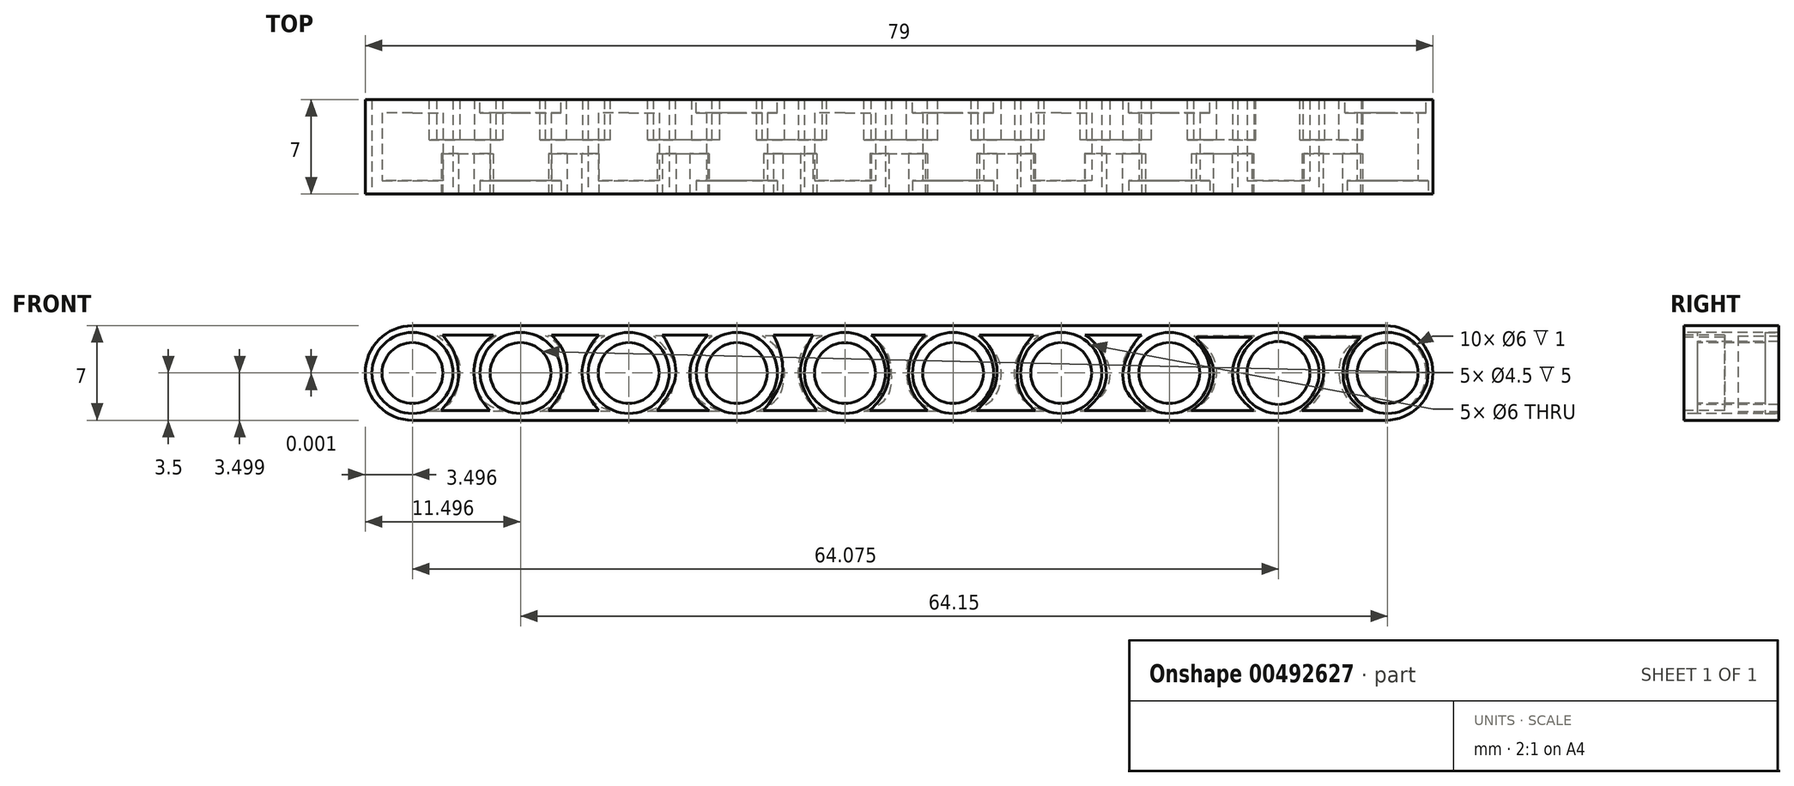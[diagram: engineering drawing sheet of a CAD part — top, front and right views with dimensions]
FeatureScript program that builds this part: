
annotation { "Feature Type Name" : "Feature", "Feature Type Description" : "" }
export const myFeature = defineFeature(function(context is Context, id is Id, definition is map)
    precondition{}
    {
        {
            var Q0;
            Q0=qCreatedBy(makeId("Front.planeOp"),FACE);
            var sketch = newSketch(context, id + "F0", { "sketchPlane" : qUnion([Q0])});
            skLineSegment(sketch, "E0", {"start": v(-57.43, 7) * mm, "end": v(21.57, 7) * mm});
            skLineSegment(sketch, "E1", {"start": v(21.57, 7) * mm, "end": v(21.57, 0) * mm});
            skLineSegment(sketch, "E2", {"start": v(21.57, 0) * mm, "end": v(-57.43, 0) * mm});
            skLineSegment(sketch, "E3", {"start": v(-57.43, 0) * mm, "end": v(-57.43, 7) * mm});
            skLineSegment(sketch, "E4", {"start": v(-62.57, 3.5) * mm, "end": v(30.14, 3.5) * mm, "construction": true});
            skPoint(sketch, "E4.startSnap0", {"position": v(-57.43, 3.5) * mm});
            skPoint(sketch, "E4.endSnap0", {"position": v(21.57, 3.5) * mm});
            skSolve(sketch);
        }
        {
            var Q0;
            Q0 = qSketchRegion(id + "F0", true);
            extrude(context, id + "F1", {"entities" : qUnion([Q0]), "depth" : 7 * mm});
        }
        {
            var Q0;
            Q0=makeQuery(id+"F1.opExtrude","CAP_FACE",FACE,{"disambiguationData":[OSD([sQuery(id+"F0.wireOp",EDGE,"E0"),sQuery(id+"F0.wireOp",EDGE,"E1"),sQuery(id+"F0.wireOp",EDGE,"E2"),sQuery(id+"F0.wireOp",EDGE,"E3")])],"isStart":false});
            var sketch = newSketch(context, id + "F2", { "sketchPlane" : qUnion([Q0])});
            skPoint(sketch, "E5.startSnap0", {"position": v(-57.43, 3.5) * mm});
            skPoint(sketch, "E5.endSnap0", {"position": v(21.57, 3.5) * mm});
            skCircle(sketch, "E6", {"center": v(18.22, 3.5) * mm, "radius": 2.25 * mm});
            skCircle(sketch, "E7.MirrorC", {"center": v(10.14, 3.5) * mm, "radius": 2.32 * mm});
            skCircle(sketch, "E8.MirrorC", {"center": v(2.07, 3.5) * mm, "radius": 2.25 * mm});
            skCircle(sketch, "E9.MirrorC", {"center": v(-5.93, 3.5) * mm, "radius": 2.25 * mm});
            skCircle(sketch, "E10.MirrorC", {"center": v(-13.93, 3.5) * mm, "radius": 2.25 * mm});
            skCircle(sketch, "E11.MirrorC", {"center": v(-21.93, 3.5) * mm, "radius": 2.25 * mm});
            skCircle(sketch, "E12.MirrorC", {"center": v(-29.93, 3.5) * mm, "radius": 2.25 * mm});
            skCircle(sketch, "E13.MirrorC", {"center": v(-37.93, 3.5) * mm, "radius": 2.25 * mm});
            skCircle(sketch, "E14.MirrorC", {"center": v(-45.93, 3.5) * mm, "radius": 2.25 * mm});
            skCircle(sketch, "E15.MirrorC", {"center": v(-53.93, 3.5) * mm, "radius": 2.25 * mm});
            skCircle(sketch, "E16", {"center": v(18.22, 3.5) * mm, "radius": 3 * mm});
            skCircle(sketch, "E17", {"center": v(10.14, 3.5) * mm, "radius": 3 * mm});
            skCircle(sketch, "E18", {"center": v(2.07, 3.5) * mm, "radius": 3 * mm});
            skCircle(sketch, "E19", {"center": v(-5.93, 3.5) * mm, "radius": 3 * mm});
            skCircle(sketch, "E20", {"center": v(-13.93, 3.5) * mm, "radius": 3 * mm});
            skCircle(sketch, "E21", {"center": v(-21.93, 3.5) * mm, "radius": 3 * mm});
            skCircle(sketch, "E22", {"center": v(-29.93, 3.5) * mm, "radius": 3 * mm});
            skCircle(sketch, "E23", {"center": v(-37.93, 3.5) * mm, "radius": 3 * mm});
            skCircle(sketch, "E24", {"center": v(-45.93, 3.5) * mm, "radius": 3 * mm});
            skCircle(sketch, "E25", {"center": v(-53.93, 3.5) * mm, "radius": 3 * mm});
            skSolve(sketch);
        }
        {
            var Q0;
            Q0=makeQuery(id+"F2.imprint","IMPRINT",FACE,{"disambiguationData":[TD([[makeQuery(id+"F2.imprint","IMPRINT",EDGE,{"derivedFrom":sQuery(id+"F2.wireOp",EDGE,"E6")}),-1.0]])]});
            var sketch = newSketch(context, id + "F3", { "sketchPlane" : qUnion([Q0])});
            skSolve(sketch);
        }
        {
            var Q0;
            Q0=makeQuery(id+"F2.imprint","IMPRINT",FACE,{"disambiguationData":[TD([[makeQuery(id+"F2.imprint","IMPRINT",EDGE,{"derivedFrom":sQuery(id+"F2.wireOp",EDGE,"E6")}),-1.0]])]});
            var Q1;
            Q1=makeQuery(id+"F2.imprint","IMPRINT",FACE,{"disambiguationData":[TD([[makeQuery(id+"F2.imprint","IMPRINT",EDGE,{"derivedFrom":sQuery(id+"F2.wireOp",EDGE,"E7.MirrorC")}),1.0]])]});
            var Q2;
            Q2=makeQuery(id+"F2.imprint","IMPRINT",FACE,{"disambiguationData":[TD([[makeQuery(id+"F2.imprint","IMPRINT",EDGE,{"derivedFrom":sQuery(id+"F2.wireOp",EDGE,"E8.MirrorC")}),-1.0]])]});
            var Q3;
            Q3=makeQuery(id+"F2.imprint","IMPRINT",FACE,{"disambiguationData":[TD([[makeQuery(id+"F2.imprint","IMPRINT",EDGE,{"derivedFrom":sQuery(id+"F2.wireOp",EDGE,"E9.MirrorC")}),1.0]])]});
            var Q4;
            Q4=makeQuery(id+"F2.imprint","IMPRINT",FACE,{"disambiguationData":[TD([[makeQuery(id+"F2.imprint","IMPRINT",EDGE,{"derivedFrom":sQuery(id+"F2.wireOp",EDGE,"E10.MirrorC")}),-1.0]])]});
            var Q5;
            Q5=makeQuery(id+"F2.imprint","IMPRINT",FACE,{"disambiguationData":[TD([[makeQuery(id+"F2.imprint","IMPRINT",EDGE,{"derivedFrom":sQuery(id+"F2.wireOp",EDGE,"E11.MirrorC")}),1.0]])]});
            var Q6;
            Q6=makeQuery(id+"F2.imprint","IMPRINT",FACE,{"disambiguationData":[TD([[makeQuery(id+"F2.imprint","IMPRINT",EDGE,{"derivedFrom":sQuery(id+"F2.wireOp",EDGE,"E12.MirrorC")}),-1.0]])]});
            var Q7;
            Q7=makeQuery(id+"F2.imprint","IMPRINT",FACE,{"disambiguationData":[TD([[makeQuery(id+"F2.imprint","IMPRINT",EDGE,{"derivedFrom":sQuery(id+"F2.wireOp",EDGE,"E13.MirrorC")}),1.0]])]});
            var Q8;
            Q8=makeQuery(id+"F2.imprint","IMPRINT",FACE,{"disambiguationData":[TD([[makeQuery(id+"F2.imprint","IMPRINT",EDGE,{"derivedFrom":sQuery(id+"F2.wireOp",EDGE,"E14.MirrorC")}),-1.0]])]});
            var Q9;
            Q9=makeQuery(id+"F2.imprint","IMPRINT",FACE,{"disambiguationData":[TD([[makeQuery(id+"F2.imprint","IMPRINT",EDGE,{"derivedFrom":sQuery(id+"F2.wireOp",EDGE,"E15.MirrorC")}),1.0]])]});
            extrude(context, id + "F4", {"entities" : qUnion([Q0, Q1, Q2, Q3, Q4, Q5, Q6, Q7, Q8, Q9]), "operationType" : NewBodyOperationType.REMOVE, "oppositeDirection" : true, "depth" : 1 * mm});
        }
        {
            var Q0;
            Q0=makeQuery(id+"F2.imprint","IMPRINT",FACE,{"disambiguationData":[TD([[makeQuery(id+"F2.imprint","IMPRINT",EDGE,{"derivedFrom":sQuery(id+"F2.wireOp",EDGE,"E15.MirrorC")}),-1.0]])]});
            var Q1;
            Q1=makeQuery(id+"F2.imprint","IMPRINT",FACE,{"disambiguationData":[TD([[makeQuery(id+"F2.imprint","IMPRINT",EDGE,{"derivedFrom":sQuery(id+"F2.wireOp",EDGE,"E14.MirrorC")}),1.0]])]});
            var Q2;
            Q2=makeQuery(id+"F2.imprint","IMPRINT",FACE,{"disambiguationData":[TD([[makeQuery(id+"F2.imprint","IMPRINT",EDGE,{"derivedFrom":sQuery(id+"F2.wireOp",EDGE,"E13.MirrorC")}),-1.0]])]});
            var Q3;
            Q3=makeQuery(id+"F2.imprint","IMPRINT",FACE,{"disambiguationData":[TD([[makeQuery(id+"F2.imprint","IMPRINT",EDGE,{"derivedFrom":sQuery(id+"F2.wireOp",EDGE,"E12.MirrorC")}),1.0]])]});
            var Q4;
            Q4=makeQuery(id+"F2.imprint","IMPRINT",FACE,{"disambiguationData":[TD([[makeQuery(id+"F2.imprint","IMPRINT",EDGE,{"derivedFrom":sQuery(id+"F2.wireOp",EDGE,"E11.MirrorC")}),-1.0]])]});
            var Q5;
            Q5=makeQuery(id+"F2.imprint","IMPRINT",FACE,{"disambiguationData":[TD([[makeQuery(id+"F2.imprint","IMPRINT",EDGE,{"derivedFrom":sQuery(id+"F2.wireOp",EDGE,"E10.MirrorC")}),1.0]])]});
            var Q6;
            Q6=makeQuery(id+"F2.imprint","IMPRINT",FACE,{"disambiguationData":[TD([[makeQuery(id+"F2.imprint","IMPRINT",EDGE,{"derivedFrom":sQuery(id+"F2.wireOp",EDGE,"E9.MirrorC")}),-1.0]])]});
            var Q7;
            Q7=makeQuery(id+"F2.imprint","IMPRINT",FACE,{"disambiguationData":[TD([[makeQuery(id+"F2.imprint","IMPRINT",EDGE,{"derivedFrom":sQuery(id+"F2.wireOp",EDGE,"E8.MirrorC")}),1.0]])]});
            var Q8;
            Q8=makeQuery(id+"F2.imprint","IMPRINT",FACE,{"disambiguationData":[TD([[makeQuery(id+"F2.imprint","IMPRINT",EDGE,{"derivedFrom":sQuery(id+"F2.wireOp",EDGE,"E7.MirrorC")}),-1.0]])]});
            var Q9;
            Q9=makeQuery(id+"F2.imprint","IMPRINT",FACE,{"disambiguationData":[TD([[makeQuery(id+"F2.imprint","IMPRINT",EDGE,{"derivedFrom":sQuery(id+"F2.wireOp",EDGE,"E6")}),1.0]])]});
            extrude(context, id + "F5", {"entities" : qUnion([Q0, Q1, Q2, Q3, Q4, Q5, Q6, Q7, Q8, Q9]), "operationType" : NewBodyOperationType.REMOVE, "oppositeDirection" : true, "depth" : 8 * mm});
        }
        {
            var Q0;
            Q0=makeQuery(id+"F1.opExtrude","SWEPT_EDGE",EDGE,{"disambiguationData":[OSD([sQuery(id+"F0.wireOp",EDGE,"E0"),sQuery(id+"F0.wireOp",EDGE,"E1")])]});
            var Q1;
            Q1=makeQuery(id+"F1.opExtrude","SWEPT_EDGE",EDGE,{"disambiguationData":[OSD([sQuery(id+"F0.wireOp",EDGE,"E0"),sQuery(id+"F0.wireOp",EDGE,"E3")])]});
            var Q2;
            Q2=makeQuery(id+"F1.opExtrude","SWEPT_EDGE",EDGE,{"disambiguationData":[OSD([sQuery(id+"F0.wireOp",EDGE,"E1"),sQuery(id+"F0.wireOp",EDGE,"E2")])]});
            var Q3;
            Q3=makeQuery(id+"F1.opExtrude","SWEPT_EDGE",EDGE,{"disambiguationData":[OSD([sQuery(id+"F0.wireOp",EDGE,"E2"),sQuery(id+"F0.wireOp",EDGE,"E3")])]});
            fillet(context, id + "F6", {"entities" : qUnion([Q0, Q1, Q2, Q3]), "radius" : 3.5 * mm, "tangentPropagation" : true, "allowEdgeOverflow" : false});
        }
        {
            var Q0;
            Q0=makeQuery(id+"F1.opExtrude","CAP_FACE",FACE,{"disambiguationData":[OSD([sQuery(id+"F0.wireOp",EDGE,"E0"),sQuery(id+"F0.wireOp",EDGE,"E1"),sQuery(id+"F0.wireOp",EDGE,"E2"),sQuery(id+"F0.wireOp",EDGE,"E3")])],"isStart":true});
            var sketch = newSketch(context, id + "F7", { "sketchPlane" : qUnion([Q0])});
            skPoint(sketch, "E26", {"position": v(-10.14, 3.5) * mm});
            skPoint(sketch, "E27", {"position": v(-2.07, 3.5) * mm});
            skPoint(sketch, "E28", {"position": v(5.93, 3.5) * mm});
            skPoint(sketch, "E29", {"position": v(13.93, 3.5) * mm});
            skPoint(sketch, "E30", {"position": v(21.93, 3.5) * mm});
            skPoint(sketch, "E31", {"position": v(29.93, 3.5) * mm});
            skPoint(sketch, "E32", {"position": v(37.93, 3.5) * mm});
            skPoint(sketch, "E33", {"position": v(45.93, 3.5) * mm});
            skPoint(sketch, "E34", {"position": v(53.93, 3.5) * mm});
            skPoint(sketch, "E35", {"position": v(-18.07, 3.5) * mm});
            skCircle(sketch, "E36", {"center": v(-18.07, 3.5) * mm, "radius": 3 * mm});
            skCircle(sketch, "E37", {"center": v(-10.14, 3.5) * mm, "radius": 3 * mm});
            skCircle(sketch, "E38", {"center": v(-2.07, 3.5) * mm, "radius": 3 * mm});
            skCircle(sketch, "E39", {"center": v(5.93, 3.5) * mm, "radius": 3 * mm});
            skCircle(sketch, "E40", {"center": v(13.93, 3.5) * mm, "radius": 3 * mm});
            skCircle(sketch, "E41", {"center": v(21.93, 3.5) * mm, "radius": 3 * mm});
            skCircle(sketch, "E42", {"center": v(29.93, 3.5) * mm, "radius": 3 * mm});
            skCircle(sketch, "E43", {"center": v(37.93, 3.5) * mm, "radius": 3 * mm});
            skCircle(sketch, "E44", {"center": v(45.93, 3.5) * mm, "radius": 3 * mm});
            skCircle(sketch, "E45", {"center": v(53.93, 3.5) * mm, "radius": 3 * mm});
            skSolve(sketch);
        }
        {
            var Q0;
            Q0=makeQuery(id+"F7.imprint","IMPRINT",FACE,{"disambiguationData":[TD([[makeQuery(id+"F7.imprint","IMPRINT",EDGE,{"derivedFrom":sQuery(id+"F7.wireOp",EDGE,"E36")}),1.0]])]});
            var Q1;
            Q1=makeQuery(id+"F7.imprint","IMPRINT",FACE,{"disambiguationData":[TD([[makeQuery(id+"F7.imprint","IMPRINT",EDGE,{"derivedFrom":sQuery(id+"F7.wireOp",EDGE,"E37")}),1.0]])]});
            var Q2;
            Q2=makeQuery(id+"F7.imprint","IMPRINT",FACE,{"disambiguationData":[TD([[makeQuery(id+"F7.imprint","IMPRINT",EDGE,{"derivedFrom":sQuery(id+"F7.wireOp",EDGE,"E38")}),1.0]])]});
            var Q3;
            Q3=makeQuery(id+"F7.imprint","IMPRINT",FACE,{"disambiguationData":[TD([[makeQuery(id+"F7.imprint","IMPRINT",EDGE,{"derivedFrom":sQuery(id+"F7.wireOp",EDGE,"E39")}),1.0]])]});
            var Q4;
            Q4=makeQuery(id+"F7.imprint","IMPRINT",FACE,{"disambiguationData":[TD([[makeQuery(id+"F7.imprint","IMPRINT",EDGE,{"derivedFrom":sQuery(id+"F7.wireOp",EDGE,"E40")}),1.0]])]});
            var Q5;
            Q5=makeQuery(id+"F7.imprint","IMPRINT",FACE,{"disambiguationData":[TD([[makeQuery(id+"F7.imprint","IMPRINT",EDGE,{"derivedFrom":sQuery(id+"F7.wireOp",EDGE,"E41")}),1.0]])]});
            var Q6;
            Q6=makeQuery(id+"F7.imprint","IMPRINT",FACE,{"disambiguationData":[TD([[makeQuery(id+"F7.imprint","IMPRINT",EDGE,{"derivedFrom":sQuery(id+"F7.wireOp",EDGE,"E42")}),1.0]])]});
            var Q7;
            Q7=makeQuery(id+"F7.imprint","IMPRINT",FACE,{"disambiguationData":[TD([[makeQuery(id+"F7.imprint","IMPRINT",EDGE,{"derivedFrom":sQuery(id+"F7.wireOp",EDGE,"E43")}),1.0]])]});
            var Q8;
            Q8=makeQuery(id+"F7.imprint","IMPRINT",FACE,{"disambiguationData":[TD([[makeQuery(id+"F7.imprint","IMPRINT",EDGE,{"derivedFrom":sQuery(id+"F7.wireOp",EDGE,"E44")}),1.0]])]});
            var Q9;
            Q9=makeQuery(id+"F7.imprint","IMPRINT",FACE,{"disambiguationData":[TD([[makeQuery(id+"F7.imprint","IMPRINT",EDGE,{"derivedFrom":sQuery(id+"F7.wireOp",EDGE,"E45")}),1.0]])]});
            extrude(context, id + "F8", {"entities" : qUnion([Q0, Q1, Q2, Q3, Q4, Q5, Q6, Q7, Q8, Q9]), "operationType" : NewBodyOperationType.REMOVE, "oppositeDirection" : true, "depth" : 1 * mm});
        }
        {
            var Q0;
            {var subQ0=sQuery(id+"F0.wireOp",EDGE,"E0");var subQ1=sQuery(id+"F0.wireOp",EDGE,"E3");var subQ2=sQuery(id+"F0.wireOp",EDGE,"E1");var subQ3=sQuery(id+"F0.wireOp",EDGE,"E2");Q0=makeQuery(id+"F4.boolean.opBoolean","SPLIT",FACE,{"disambiguationData":[TD([makeQuery(id+"F1.opExtrude","SWEPT_FACE",FACE,{"disambiguationData":[OSD([subQ0])]})])],"derivedFrom":makeQuery(id+"F1.opExtrude","CAP_FACE",FACE,{"disambiguationData":[OSD([subQ0,subQ2,subQ3,subQ1])],"isStart":false})});}
            var sketch = newSketch(context, id + "F9", { "sketchPlane" : qUnion([Q0])});
            skLineSegment(sketch, "E46", {"start": v(-51.71, 6.32) * mm, "end": v(-47.97, 6.32) * mm});
            skLineSegment(sketch, "E47", {"start": v(-51.82, 0.71) * mm, "end": v(-48.22, 0.71) * mm});
            skFitSpline(sketch, "E48", {"points": [v(-51.71, 6.32) * mm, v(-50.89, 5.11) * mm, v(-50.6, 2.7) * mm, v(-51.82, 0.71) * mm], "startDerivative": vector(3.7, -5.12) * mm, "endDerivative": vector(-4.17, -5.13) * mm});
            skFitSpline(sketch, "E49", {"points": [v(-48.22, 0.71) * mm, v(-49.22, 2.32) * mm, v(-49.16, 4.8) * mm, v(-47.97, 6.32) * mm], "startDerivative": vector(-3.67, 4.38) * mm, "endDerivative": vector(4.4, 3.55) * mm});
            skLineSegment(sketch, "E50", {"start": v(-43.65, 6.32) * mm, "end": v(-40.16, 6.32) * mm});
            skLineSegment(sketch, "E51", {"start": v(-43.86, 0.71) * mm, "end": v(-40.16, 0.71) * mm});
            skFitSpline(sketch, "E52", {"points": [v(-43.65, 6.32) * mm, v(-42.7, 4.93) * mm, v(-42.64, 2.7) * mm, v(-43.86, 0.71) * mm], "startDerivative": vector(3.54, -3.64) * mm, "endDerivative": vector(-4.12, -5.15) * mm});
            skFitSpline(sketch, "E53", {"points": [v(-40.16, 6.32) * mm, v(-41.2, 4.58) * mm, v(-41.26, 2.6) * mm, v(-40.16, 0.71) * mm], "startDerivative": vector(-3.86, -4.46) * mm, "endDerivative": vector(3.88, -5.17) * mm});
            skLineSegment(sketch, "E54", {"start": v(-35.46, 6.32) * mm, "end": v(-32.1, 6.32) * mm});
            skLineSegment(sketch, "E55", {"start": v(-35.85, 0.71) * mm, "end": v(-31.98, 0.71) * mm});
            skFitSpline(sketch, "E56", {"points": [v(-35.46, 6.32) * mm, v(-34.69, 4.86) * mm, v(-34.52, 2.98) * mm, v(-35.85, 0.71) * mm], "startDerivative": vector(2.99, -4.05) * mm, "endDerivative": vector(-4.42, -5.82) * mm});
            skFitSpline(sketch, "E57", {"points": [v(-31.98, 0.71) * mm, v(-33.03, 1.77) * mm, v(-33.36, 3.98) * mm, v(-32.1, 6.32) * mm], "startDerivative": vector(-4.1, 3.03) * mm, "endDerivative": vector(4.46, 5.51) * mm});
            skLineSegment(sketch, "E58", {"start": v(-27.23, 6.32) * mm, "end": v(-24.3, 6.32) * mm});
            skLineSegment(sketch, "E59", {"start": v(-27.95, 0.71) * mm, "end": v(-24.03, 0.71) * mm});
            skFitSpline(sketch, "E60", {"points": [v(-27.23, 6.32) * mm, v(-26.67, 4.83) * mm, v(-26.67, 2.87) * mm, v(-27.95, 0.71) * mm], "startDerivative": vector(2.25, -4.24) * mm, "endDerivative": vector(-4.17, -5.54) * mm});
            skFitSpline(sketch, "E61", {"points": [v(-24.03, 0.71) * mm, v(-24.87, 2.05) * mm, v(-25.22, 3.88) * mm, v(-24.3, 6.32) * mm], "startDerivative": vector(-3.04, 4.16) * mm, "endDerivative": vector(3.33, 6.07) * mm});
            skLineSegment(sketch, "E62", {"start": v(-19.98, 6.32) * mm, "end": v(-16, 6.32) * mm});
            skLineSegment(sketch, "E63", {"start": v(-20.07, 0.71) * mm, "end": v(-15.84, 0.71) * mm});
            skLineSegment(sketch, "E64", {"start": v(-12, 6.32) * mm, "end": v(-7.98, 6.32) * mm});
            skLineSegment(sketch, "E65", {"start": v(-12.18, 0.71) * mm, "end": v(-7.86, 0.71) * mm});
            skLineSegment(sketch, "E66", {"start": v(-4.2, 0.71) * mm, "end": v(0.29, 0.71) * mm});
            skLineSegment(sketch, "E67", {"start": v(-4.16, 6.32) * mm, "end": v(0, 6.32) * mm});
            skLineSegment(sketch, "E68", {"start": v(4.04, 6.13) * mm, "end": v(8.18, 6.13) * mm});
            skLineSegment(sketch, "E69", {"start": v(12.03, 6.13) * mm, "end": v(16.2, 6.13) * mm});
            skLineSegment(sketch, "E70", {"start": v(3.7, 0.71) * mm, "end": v(8.3, 0.71) * mm});
            skLineSegment(sketch, "E71", {"start": v(11.87, 0.72) * mm, "end": v(16.35, 0.72) * mm});
            skFitSpline(sketch, "E72", {"points": [v(-19.98, 6.32) * mm, v(-18.87, 4.64) * mm, v(-18.87, 2.4) * mm, v(-20.07, 0.71) * mm], "startDerivative": vector(4.14, -4.17) * mm, "endDerivative": vector(-4.29, -4.54) * mm});
            skFitSpline(sketch, "E73", {"points": [v(-15.84, 0.71) * mm, v(-17.01, 2.27) * mm, v(-17.07, 4.58) * mm, v(-16, 6.32) * mm], "startDerivative": vector(-4.23, 4.22) * mm, "endDerivative": vector(4.02, 4.31) * mm});
            skFitSpline(sketch, "E74", {"points": [v(-12, 6.32) * mm, v(-10.86, 4.64) * mm, v(-10.89, 2.43) * mm, v(-12.18, 0.71) * mm], "startDerivative": vector(4.29, -4.18) * mm, "endDerivative": vector(-4.55, -4.57) * mm});
            skFitSpline(sketch, "E75", {"points": [v(-7.86, 0.71) * mm, v(-9, 2.18) * mm, v(-9.02, 4.64) * mm, v(-7.98, 6.32) * mm], "startDerivative": vector(-4.22, 3.93) * mm, "endDerivative": vector(3.92, 4.1) * mm});
            skFitSpline(sketch, "E76", {"points": [v(-4.16, 6.32) * mm, v(-2.93, 4.92) * mm, v(-2.71, 2.59) * mm, v(-4.2, 0.71) * mm], "startDerivative": vector(4.68, -3.3) * mm, "endDerivative": vector(-5.27, -4.75) * mm});
            skFitSpline(sketch, "E77", {"points": [v(0, 6.32) * mm, v(-1.04, 4.73) * mm, v(-1.26, 2.53) * mm, v(0.29, 0.71) * mm], "startDerivative": vector(-3.81, -4.06) * mm, "endDerivative": vector(5.53, -4.6) * mm});
            skFitSpline(sketch, "E78", {"points": [v(3.7, 0.71) * mm, v(4.8, 1.74) * mm, v(5.3, 3.88) * mm, v(4.04, 6.13) * mm], "startDerivative": vector(4.2, 2.93) * mm, "endDerivative": vector(-4.56, 5.79) * mm});
            skFitSpline(sketch, "E79", {"points": [v(8.18, 6.13) * mm, v(7.01, 4.7) * mm, v(6.92, 2.4) * mm, v(8.3, 0.71) * mm], "startDerivative": vector(-4.34, -3.96) * mm, "endDerivative": vector(5, -4.38) * mm});
            skFitSpline(sketch, "E80", {"points": [v(11.87, 0.72) * mm, v(13.23, 2.37) * mm, v(13.32, 4.6) * mm, v(12.03, 6.13) * mm], "startDerivative": vector(4.77, 4.39) * mm, "endDerivative": vector(-4.87, 4.13) * mm});
            skFitSpline(sketch, "E81", {"points": [v(16.2, 6.13) * mm, v(15.1, 4.55) * mm, v(15.12, 2.3) * mm, v(16.35, 0.72) * mm], "startDerivative": vector(-4.09, -4.4) * mm, "endDerivative": vector(4.45, -4.3) * mm});
            skSolve(sketch);
        }
        {
            var Q0;
            Q0=makeQuery(id+"F9.imprint","IMPRINT",FACE,{"disambiguationData":[TD([[makeQuery(id+"F9.imprint","IMPRINT",EDGE,{"derivedFrom":sQuery(id+"F9.wireOp",EDGE,"E46")}),-1.0]])]});
            var Q1;
            Q1=makeQuery(id+"F9.imprint","IMPRINT",FACE,{"disambiguationData":[TD([[makeQuery(id+"F9.imprint","IMPRINT",EDGE,{"derivedFrom":sQuery(id+"F9.wireOp",EDGE,"E50")}),-1.0]])]});
            var Q2;
            Q2=makeQuery(id+"F9.imprint","IMPRINT",FACE,{"disambiguationData":[TD([[makeQuery(id+"F9.imprint","IMPRINT",EDGE,{"derivedFrom":sQuery(id+"F9.wireOp",EDGE,"E54")}),-1.0]])]});
            var Q3;
            Q3=makeQuery(id+"F9.imprint","IMPRINT",FACE,{"disambiguationData":[TD([[makeQuery(id+"F9.imprint","IMPRINT",EDGE,{"derivedFrom":sQuery(id+"F9.wireOp",EDGE,"E58")}),-1.0]])]});
            var Q4;
            Q4=makeQuery(id+"F9.imprint","IMPRINT",FACE,{"disambiguationData":[TD([[makeQuery(id+"F9.imprint","IMPRINT",EDGE,{"derivedFrom":sQuery(id+"F9.wireOp",EDGE,"E62")}),-1.0]])]});
            var Q5;
            Q5=makeQuery(id+"F9.imprint","IMPRINT",FACE,{"disambiguationData":[TD([[makeQuery(id+"F9.imprint","IMPRINT",EDGE,{"derivedFrom":sQuery(id+"F9.wireOp",EDGE,"E64")}),-1.0]])]});
            var Q6;
            Q6=makeQuery(id+"F9.imprint","IMPRINT",FACE,{"disambiguationData":[TD([[makeQuery(id+"F9.imprint","IMPRINT",EDGE,{"derivedFrom":sQuery(id+"F9.wireOp",EDGE,"E66")}),1.0]])]});
            var Q7;
            Q7=makeQuery(id+"F9.imprint","IMPRINT",FACE,{"disambiguationData":[TD([[makeQuery(id+"F9.imprint","IMPRINT",EDGE,{"derivedFrom":sQuery(id+"F9.wireOp",EDGE,"E68")}),-1.0]])]});
            var Q8;
            Q8=makeQuery(id+"F9.imprint","IMPRINT",FACE,{"disambiguationData":[TD([[makeQuery(id+"F9.imprint","IMPRINT",EDGE,{"derivedFrom":sQuery(id+"F9.wireOp",EDGE,"E69")}),-1.0]])]});
            extrude(context, id + "F10", {"entities" : qUnion([Q0, Q1, Q2, Q3, Q4, Q5, Q6, Q7, Q8]), "operationType" : NewBodyOperationType.REMOVE, "oppositeDirection" : true, "depth" : 3 * mm, "offsetDistance" : 25 * mm});
        }
        {
            var Q0;
            Q0=makeQuery(id+"F1.opExtrude","CAP_FACE",FACE,{"disambiguationData":[OSD([sQuery(id+"F0.wireOp",EDGE,"E0"),sQuery(id+"F0.wireOp",EDGE,"E1"),sQuery(id+"F0.wireOp",EDGE,"E2"),sQuery(id+"F0.wireOp",EDGE,"E3")])],"isStart":true});
            var sketch = newSketch(context, id + "F11", { "sketchPlane" : qUnion([Q0])});
            skLineSegment(sketch, "E82", {"start": v(-16.31, 6.25) * mm, "end": v(-11.99, 6.25) * mm});
            skLineSegment(sketch, "E83", {"start": v(-8.36, 6.25) * mm, "end": v(-3.88, 6.25) * mm});
            skLineSegment(sketch, "E84", {"start": v(0, 6.25) * mm, "end": v(4.05, 6.25) * mm});
            skLineSegment(sketch, "E85", {"start": v(7.61, 6.25) * mm, "end": v(12.1, 6.25) * mm});
            skLineSegment(sketch, "E86", {"start": v(15.82, 6.25) * mm, "end": v(19.99, 6.25) * mm});
            skLineSegment(sketch, "E87", {"start": v(23.62, 6.25) * mm, "end": v(28.07, 6.25) * mm});
            skLineSegment(sketch, "E88", {"start": v(31.76, 6.25) * mm, "end": v(36.09, 6.25) * mm});
            skLineSegment(sketch, "E89", {"start": v(39.72, 6.25) * mm, "end": v(44.07, 6.25) * mm});
            skLineSegment(sketch, "E90", {"start": v(47.73, 6.25) * mm, "end": v(52.12, 6.25) * mm});
            skLineSegment(sketch, "E91", {"start": v(-16.4, 0.66) * mm, "end": v(-11.74, 0.66) * mm});
            skLineSegment(sketch, "E92", {"start": v(-8.45, 0.66) * mm, "end": v(-3.43, 0.66) * mm});
            skLineSegment(sketch, "E93", {"start": v(-0.74, 0.66) * mm, "end": v(4.52, 0.66) * mm});
            skLineSegment(sketch, "E94", {"start": v(7.2, 0.66) * mm, "end": v(12.6, 0.66) * mm});
            skLineSegment(sketch, "E95", {"start": v(15.08, 0.66) * mm, "end": v(20.53, 0.66) * mm});
            skLineSegment(sketch, "E96", {"start": v(23.28, 0.66) * mm, "end": v(28.46, 0.66) * mm});
            skLineSegment(sketch, "E97", {"start": v(31.2, 0.66) * mm, "end": v(36.55, 0.66) * mm});
            skLineSegment(sketch, "E98", {"start": v(39.29, 0.66) * mm, "end": v(44.51, 0.66) * mm});
            skLineSegment(sketch, "E99", {"start": v(47.22, 0.66) * mm, "end": v(52.7, 0.66) * mm});
            skFitSpline(sketch, "E100", {"points": [v(-16.31, 6.25) * mm, v(-14.71, 4.46) * mm, v(-15.15, 1.7) * mm, v(-16.4, 0.66) * mm], "startDerivative": vector(5.92, -4.34) * mm, "endDerivative": vector(-4.82, -2.64) * mm});
            skFitSpline(sketch, "E101", {"points": [v(-11.74, 0.66) * mm, v(-13.17, 1.8) * mm, v(-13.44, 4.4) * mm, v(-11.99, 6.25) * mm], "startDerivative": vector(-5.42, 2.86) * mm, "endDerivative": vector(5.3, 4.7) * mm});
            skFitSpline(sketch, "E102", {"points": [v(-8.36, 6.25) * mm, v(-6.92, 4.63) * mm, v(-7.14, 1.92) * mm, v(-8.45, 0.66) * mm], "startDerivative": vector(5.35, -4.1) * mm, "endDerivative": vector(-4.93, -3.25) * mm});
            skFitSpline(sketch, "E103", {"points": [v(-3.43, 0.66) * mm, v(-5.1, 1.86) * mm, v(-5.43, 4.4) * mm, v(-3.88, 6.25) * mm], "startDerivative": vector(-6.11, 2.85) * mm, "endDerivative": vector(5.76, 4.73) * mm});
            skFitSpline(sketch, "E104", {"points": [v(-0.74, 0.66) * mm, v(0.87, 1.8) * mm, v(1.3, 4.35) * mm, v(0, 6.25) * mm], "startDerivative": vector(5.82, 2.73) * mm, "endDerivative": vector(-4.97, 5.03) * mm});
            skFitSpline(sketch, "E105", {"points": [v(4.05, 6.25) * mm, v(2.52, 4.35) * mm, v(2.63, 2.25) * mm, v(4.52, 0.66) * mm], "startDerivative": vector(-5.46, -5.15) * mm, "endDerivative": vector(6.61, -4) * mm});
            skFitSpline(sketch, "E106", {"points": [v(7.2, 0.66) * mm, v(8.93, 1.75) * mm, v(9.2, 4.52) * mm, v(7.61, 6.25) * mm], "startDerivative": vector(6.47, 2.34) * mm, "endDerivative": vector(-5.9, 4.32) * mm});
            skFitSpline(sketch, "E107", {"points": [v(12.6, 0.66) * mm, v(10.8, 1.8) * mm, v(10.53, 4.4) * mm, v(12.1, 6.25) * mm], "startDerivative": vector(-6.58, 2.54) * mm, "endDerivative": vector(5.75, 4.72) * mm});
            skFitSpline(sketch, "E108", {"points": [v(15.82, 6.25) * mm, v(17.1, 4.9) * mm, v(17.38, 3.3) * mm, v(16.94, 1.8) * mm, v(15.08, 0.66) * mm], "startDerivative": vector(5.98, -4.92) * mm, "endDerivative": vector(-8, -3.56) * mm});
            skFitSpline(sketch, "E109", {"points": [v(20.53, 0.66) * mm, v(18.82, 1.7) * mm, v(18.49, 3.47) * mm, v(18.87, 5.12) * mm, v(19.99, 6.25) * mm], "startDerivative": vector(-7.68, 3.06) * mm, "endDerivative": vector(5.42, 4.3) * mm});
            skFitSpline(sketch, "E110", {"points": [v(23.28, 0.66) * mm, v(24.5, 1.31) * mm, v(25.28, 2.75) * mm, v(25.34, 4.18) * mm, v(24.84, 5.51) * mm, v(23.62, 6.25) * mm], "startDerivative": vector(6.77, 2.46) * mm, "endDerivative": vector(-7, 2.97) * mm});
            skFitSpline(sketch, "E111", {"points": [v(28.46, 0.66) * mm, v(27.05, 1.48) * mm, v(26.44, 3.02) * mm, v(26.72, 5.01) * mm, v(28.07, 6.25) * mm], "startDerivative": vector(-6.65, 2.72) * mm, "endDerivative": vector(6.26, 4.17) * mm});
            skFitSpline(sketch, "E112", {"points": [v(31.2, 0.66) * mm, v(32.8, 1.59) * mm, v(33.3, 3.25) * mm, v(32.9, 5.23) * mm, v(31.76, 6.25) * mm], "startDerivative": vector(7.21, 2.91) * mm, "endDerivative": vector(-5.63, 3.61) * mm});
            skFitSpline(sketch, "E113", {"points": [v(36.55, 0.66) * mm, v(35.11, 1.42) * mm, v(34.56, 2.8) * mm, v(34.62, 4.4) * mm, v(36.09, 6.25) * mm], "startDerivative": vector(-6.81, 2.44) * mm, "endDerivative": vector(6.34, 6.26) * mm});
            skFitSpline(sketch, "E114", {"points": [v(39.29, 0.66) * mm, v(40.7, 1.48) * mm, v(41.25, 2.7) * mm, v(41.3, 4.13) * mm, v(40.64, 5.62) * mm, v(39.72, 6.25) * mm], "startDerivative": vector(7.48, 3.17) * mm, "endDerivative": vector(-5.52, 2.74) * mm});
            skFitSpline(sketch, "E115", {"points": [v(44.51, 0.66) * mm, v(43.23, 1.37) * mm, v(42.63, 2.58) * mm, v(42.63, 4.52) * mm, v(43.23, 5.68) * mm, v(44.07, 6.25) * mm], "startDerivative": vector(-6.97, 2.88) * mm, "endDerivative": vector(5.22, 2.87) * mm});
            skFitSpline(sketch, "E116", {"points": [v(47.73, 6.25) * mm, v(48.92, 5.23) * mm, v(49.31, 3.96) * mm, v(49.2, 2.47) * mm, v(48.54, 1.31) * mm, v(47.22, 0.66) * mm], "startDerivative": vector(6.58, -4.45) * mm, "endDerivative": vector(-7.17, -2.55) * mm});
            skFitSpline(sketch, "E117", {"points": [v(52.7, 0.66) * mm, v(51.24, 1.2) * mm, v(50.64, 2.3) * mm, v(50.42, 4.02) * mm, v(50.97, 5.23) * mm, v(52.12, 6.25) * mm], "startDerivative": vector(-8.06, 1.85) * mm, "endDerivative": vector(6.17, 4.72) * mm});
            skSolve(sketch);
        }
        {
            var Q0;
            Q0 = qSketchRegion(id + "F11", true);
            extrude(context, id + "F12", {"entities" : qUnion([Q0]), "operationType" : NewBodyOperationType.REMOVE, "oppositeDirection" : true, "depth" : 3 * mm, "offsetDistance" : 25 * mm});
        }
    });
